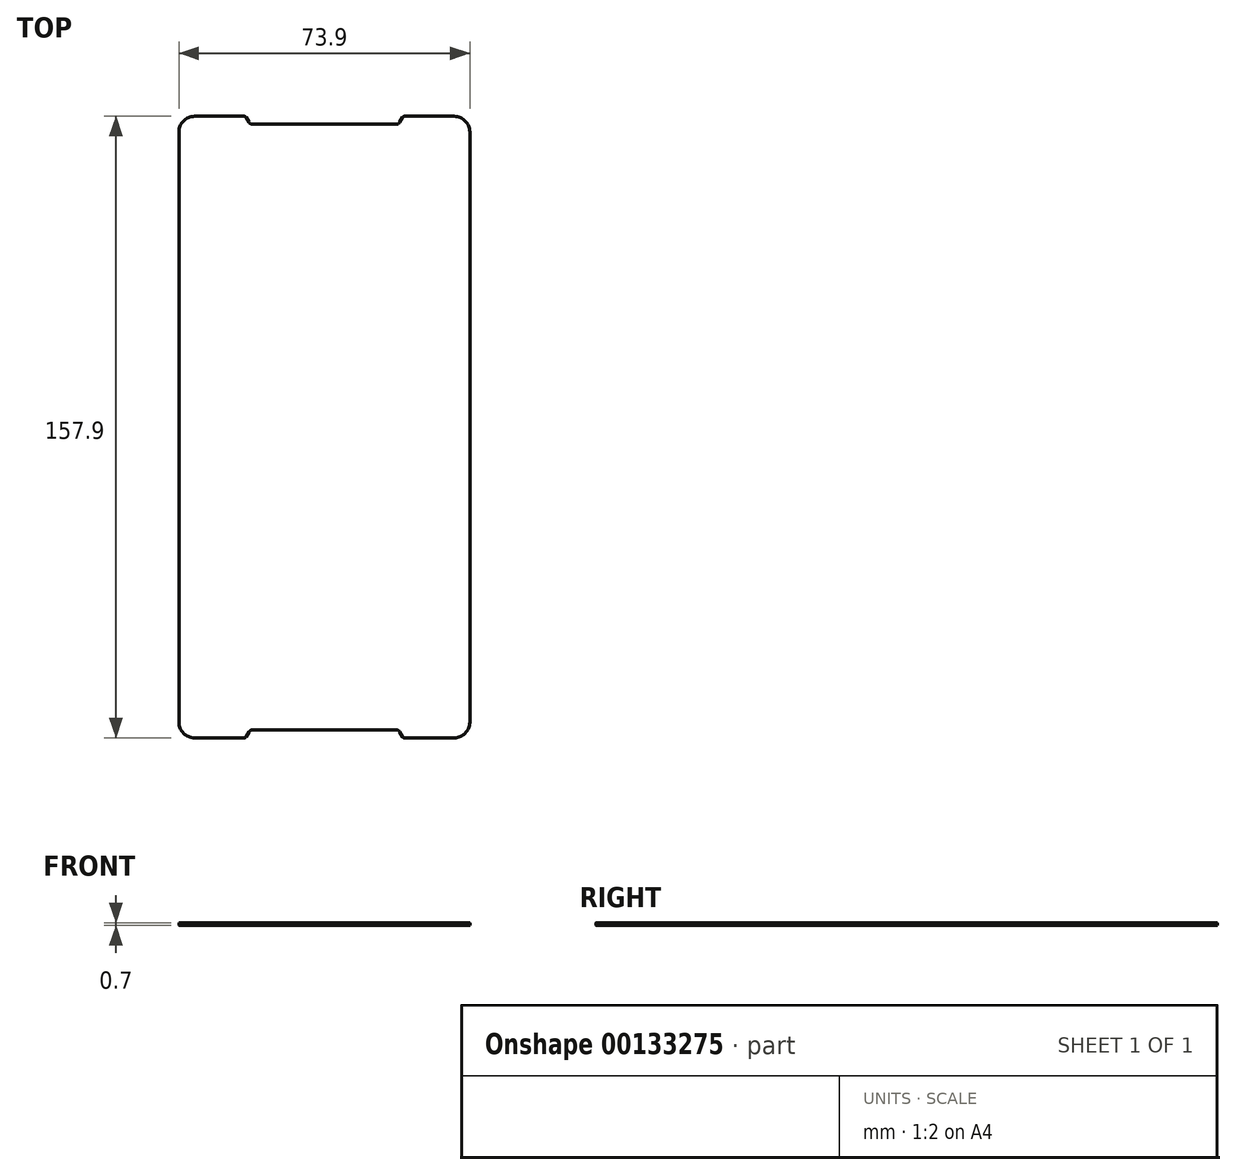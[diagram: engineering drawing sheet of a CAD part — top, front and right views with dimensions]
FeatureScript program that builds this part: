
annotation { "Feature Type Name" : "Feature", "Feature Type Description" : "" }
export const myFeature = defineFeature(function(context is Context, id is Id, definition is map)
    precondition{}
    {
        {
            var Q0;
            Q0=qCreatedBy(makeId("Top.planeOp"),FACE);
            var sketch = newSketch(context, id + "F0", { "sketchPlane" : qUnion([Q0])});
            skLineSegment(sketch, "E0", {"start": v(20, 79) * mm, "end": v(19.13, 77.5) * mm});
            skLineSegment(sketch, "E1", {"start": v(18.27, 77) * mm, "end": v(-18.27, 77) * mm});
            skLineSegment(sketch, "E2", {"start": v(-19.13, 77.5) * mm, "end": v(-20, 79) * mm});
            skPoint(sketch, "E3.visualSharp", {"position": v(-18.85, 77) * mm});
            skArc(sketch, "E3.filletArc", {"start": v(-19.13, 77.5) * mm, "mid": v(-18.77, 77.13) * mm, "end": v(-18.27, 77) * mm});
            skPoint(sketch, "E4.visualSharp", {"position": v(18.85, 77) * mm});
            skArc(sketch, "E4.filletArc", {"start": v(18.27, 77) * mm, "mid": v(18.77, 77.13) * mm, "end": v(19.13, 77.5) * mm});
            skLineSegment(sketch, "E5", {"start": v(-20, 79) * mm, "end": v(-33, 79) * mm});
            skLineSegment(sketch, "E6", {"start": v(-37, 75) * mm, "end": v(-37, 0) * mm});
            skLineSegment(sketch, "E7", {"start": v(20, 79) * mm, "end": v(33, 79) * mm});
            skLineSegment(sketch, "E8", {"start": v(37, 75) * mm, "end": v(37, 0) * mm});
            skPoint(sketch, "E9.visualSharp", {"position": v(-37, 79) * mm});
            skArc(sketch, "E9.filletArc", {"start": v(-33, 79) * mm, "mid": v(-35.83, 77.83) * mm, "end": v(-37, 75) * mm});
            skPoint(sketch, "E10.visualSharp", {"position": v(37, 79) * mm});
            skArc(sketch, "E10.filletArc", {"start": v(37, 75) * mm, "mid": v(35.83, 77.83) * mm, "end": v(33, 79) * mm});
            skArc(sketch, "E11.MirrorCS", {"start": v(18.27, -77) * mm, "mid": v(18.77, -77.13) * mm, "end": v(19.13, -77.5) * mm});
            skArc(sketch, "E12.MirrorCS", {"start": v(-19.13, -77.5) * mm, "mid": v(-18.77, -77.13) * mm, "end": v(-18.27, -77) * mm});
            skLineSegment(sketch, "E13.MirrorCS", {"start": v(-19.13, -77.5) * mm, "end": v(-20, -79) * mm});
            skLineSegment(sketch, "E14.MirrorCS", {"start": v(20, -79) * mm, "end": v(19.13, -77.5) * mm});
            skArc(sketch, "E15.MirrorCS", {"start": v(37, -75) * mm, "mid": v(35.83, -77.83) * mm, "end": v(33, -79) * mm});
            skArc(sketch, "E16.MirrorCS", {"start": v(-33, -79) * mm, "mid": v(-35.83, -77.83) * mm, "end": v(-37, -75) * mm});
            skLineSegment(sketch, "E17.MirrorCS", {"start": v(20, -79) * mm, "end": v(33, -79) * mm});
            skLineSegment(sketch, "E18.MirrorCS", {"start": v(-37, -75) * mm, "end": v(-37, 0) * mm});
            skLineSegment(sketch, "E19.MirrorCS", {"start": v(-20, -79) * mm, "end": v(-33, -79) * mm});
            skLineSegment(sketch, "E20.MirrorCS", {"start": v(37, -75) * mm, "end": v(37, 0) * mm});
            skPoint(sketch, "E21.MirrorP", {"position": v(37, -79) * mm});
            skPoint(sketch, "E22.MirrorP", {"position": v(18.85, -77) * mm});
            skPoint(sketch, "E23.MirrorP", {"position": v(-18.85, -77) * mm});
            skLineSegment(sketch, "E24.MirrorCS", {"start": v(18.27, -77) * mm, "end": v(-18.27, -77) * mm});
            skPoint(sketch, "E25.MirrorP", {"position": v(-37, -79) * mm});
            skLineSegment(sketch, "E26.0", {"start": v(20.03, 78.95) * mm, "end": v(18.87, 76.95) * mm});
            skLineSegment(sketch, "E26.1", {"start": v(20.03, 78.95) * mm, "end": v(33, 78.95) * mm});
            skArc(sketch, "E26.2", {"start": v(36.95, 75) * mm, "mid": v(35.8, 77.8) * mm, "end": v(33, 78.95) * mm});
            skLineSegment(sketch, "E26.3", {"start": v(36.95, 75) * mm, "end": v(36.95, 0) * mm});
            skLineSegment(sketch, "E26.4", {"start": v(36.95, -75) * mm, "end": v(36.95, 0) * mm});
            skLineSegment(sketch, "E26.5", {"start": v(18.87, 76.95) * mm, "end": v(-18.87, 76.95) * mm});
            skArc(sketch, "E26.6", {"start": v(36.95, -75) * mm, "mid": v(35.8, -77.8) * mm, "end": v(33, -78.95) * mm});
            skLineSegment(sketch, "E26.7", {"start": v(20.03, -78.95) * mm, "end": v(33, -78.95) * mm});
            skLineSegment(sketch, "E26.8", {"start": v(-36.95, 75) * mm, "end": v(-36.95, 0) * mm});
            skArc(sketch, "E26.9", {"start": v(-33, 78.95) * mm, "mid": v(-35.8, 77.8) * mm, "end": v(-36.95, 75) * mm});
            skLineSegment(sketch, "E26.10", {"start": v(-20.03, 78.95) * mm, "end": v(-33, 78.95) * mm});
            skLineSegment(sketch, "E26.11", {"start": v(-18.87, 76.95) * mm, "end": v(-20.03, 78.95) * mm});
            skLineSegment(sketch, "E26.12", {"start": v(-36.95, -75) * mm, "end": v(-36.95, 0) * mm});
            skArc(sketch, "E26.13", {"start": v(-33, -78.95) * mm, "mid": v(-35.8, -77.8) * mm, "end": v(-36.95, -75) * mm});
            skLineSegment(sketch, "E26.14", {"start": v(-20.03, -78.95) * mm, "end": v(-33, -78.95) * mm});
            skLineSegment(sketch, "E26.15", {"start": v(-18.87, -76.95) * mm, "end": v(-20.03, -78.95) * mm});
            skLineSegment(sketch, "E26.16", {"start": v(18.87, -76.95) * mm, "end": v(-18.87, -76.95) * mm});
            skLineSegment(sketch, "E26.17", {"start": v(20.03, -78.95) * mm, "end": v(18.87, -76.95) * mm});
            skSolve(sketch);
        }
        {
            var Q0;
            Q0=makeQuery(id+"F0.imprint","IMPRINT",FACE,{"disambiguationData":[TD([[makeQuery(id+"F0.imprint","IMPRINT",EDGE,{"derivedFrom":sQuery(id+"F0.wireOp",EDGE,"E26.0")}),1.0]])]});
            extrude(context, id + "F1", {"entities" : qUnion([Q0]), "oppositeDirection" : true, "depth" : 0.7 * mm});
        }
        {
            var Q0;
            Q0=makeQuery(id+"F1.opExtrude","SWEPT_EDGE",EDGE,{"disambiguationData":[OSD([sQuery(id+"F0.wireOp",EDGE,"E26.5"),sQuery(id+"F0.wireOp",EDGE,"E26.11")])]});
            var Q1;
            Q1=makeQuery(id+"F1.opExtrude","SWEPT_EDGE",EDGE,{"disambiguationData":[OSD([sQuery(id+"F0.wireOp",EDGE,"E26.0"),sQuery(id+"F0.wireOp",EDGE,"E26.5")])]});
            var Q2;
            Q2=makeQuery(id+"F1.opExtrude","SWEPT_EDGE",EDGE,{"disambiguationData":[OSD([sQuery(id+"F0.wireOp",EDGE,"E26.16"),sQuery(id+"F0.wireOp",EDGE,"E26.17")])]});
            var Q3;
            Q3=makeQuery(id+"F1.opExtrude","SWEPT_EDGE",EDGE,{"disambiguationData":[OSD([sQuery(id+"F0.wireOp",EDGE,"E26.15"),sQuery(id+"F0.wireOp",EDGE,"E26.16")])]});
            fillet(context, id + "F2", {"entities" : qUnion([Q0, Q1, Q2, Q3]), "radius" : 1 * mm, "tangentPropagation" : true, "allowEdgeOverflow" : false});
        }
        {
            var Q0;
            Q0=makeQuery(id+"F1.opExtrude","SWEPT_EDGE",EDGE,{"disambiguationData":[OSD([sQuery(id+"F0.wireOp",EDGE,"E26.14"),sQuery(id+"F0.wireOp",EDGE,"E26.15")])]});
            var Q1;
            Q1=makeQuery(id+"F1.opExtrude","SWEPT_EDGE",EDGE,{"disambiguationData":[OSD([sQuery(id+"F0.wireOp",EDGE,"E26.7"),sQuery(id+"F0.wireOp",EDGE,"E26.17")])]});
            var Q2;
            Q2=makeQuery(id+"F1.opExtrude","SWEPT_EDGE",EDGE,{"disambiguationData":[OSD([sQuery(id+"F0.wireOp",EDGE,"E26.0"),sQuery(id+"F0.wireOp",EDGE,"E26.1")])]});
            var Q3;
            Q3=makeQuery(id+"F1.opExtrude","SWEPT_EDGE",EDGE,{"disambiguationData":[OSD([sQuery(id+"F0.wireOp",EDGE,"E26.10"),sQuery(id+"F0.wireOp",EDGE,"E26.11")])]});
            fillet(context, id + "F3", {"entities" : qUnion([Q0, Q1, Q2, Q3]), "radius" : 0.4 * mm, "tangentPropagation" : true, "allowEdgeOverflow" : false});
        }
        {
            var Q0;
            Q0=makeQuery(id+"F1.opExtrude","CAP_EDGE",EDGE,{"disambiguationData":[OSD([sQuery(id+"F0.wireOp",EDGE,"E26.5")])],"isStart":true});
            var Q1;
            Q1=makeQuery(id+"F1.opExtrude","CAP_EDGE",EDGE,{"disambiguationData":[OSD([sQuery(id+"F0.wireOp",EDGE,"E26.5")])],"isStart":false});
            fillet(context, id + "F4", {"entities" : qUnion([Q0, Q1]), "radius" : 0.1 * mm, "tangentPropagation" : true, "allowEdgeOverflow" : false});
        }
    });
